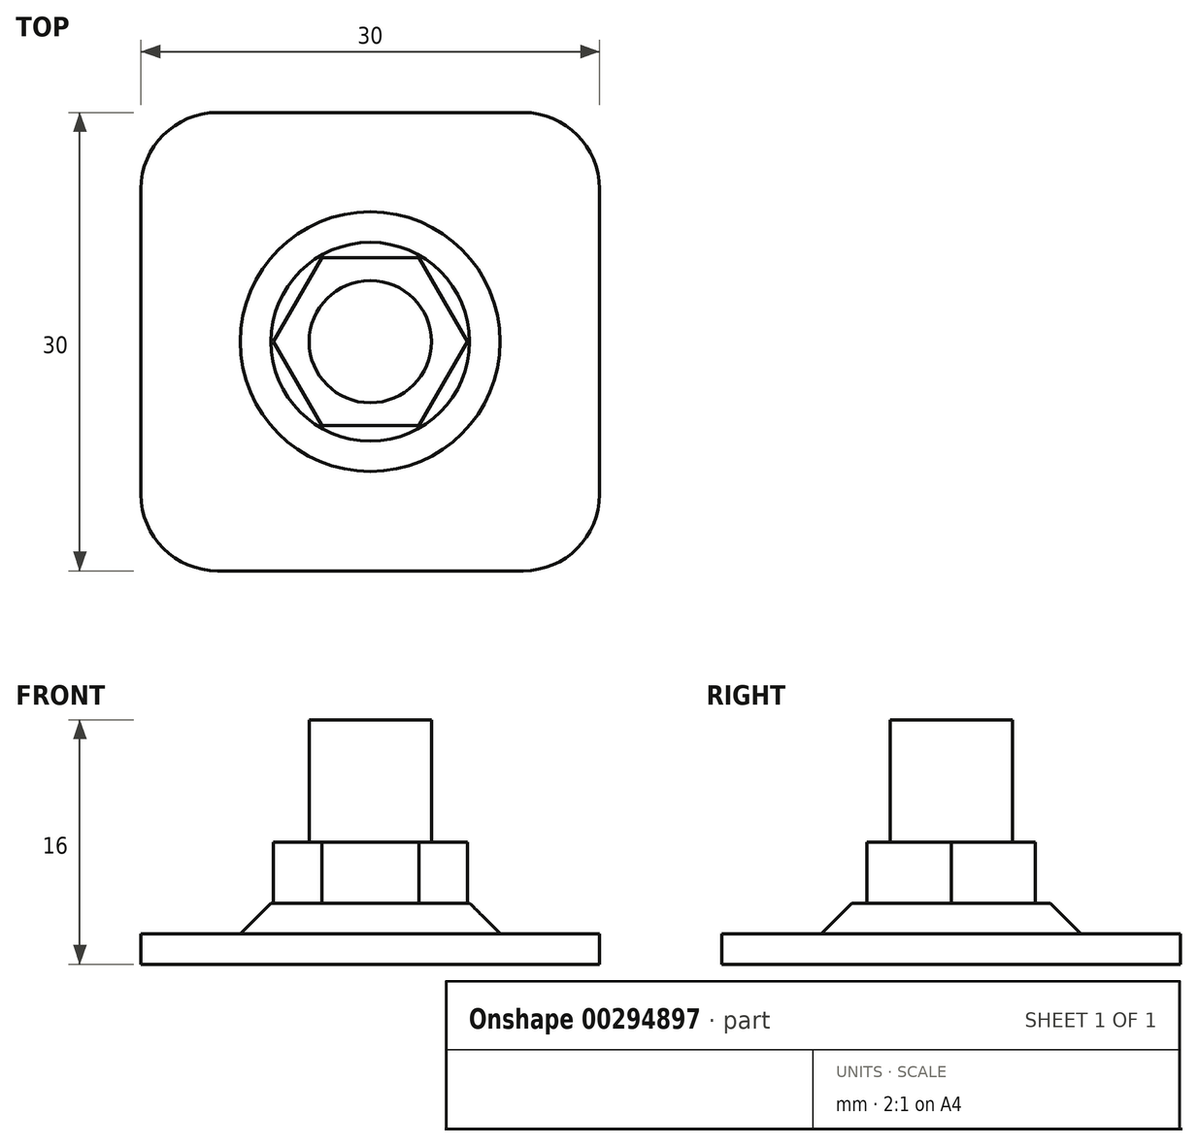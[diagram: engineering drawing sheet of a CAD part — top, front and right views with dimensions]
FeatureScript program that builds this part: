
annotation { "Feature Type Name" : "Feature", "Feature Type Description" : "" }
export const myFeature = defineFeature(function(context is Context, id is Id, definition is map)
    precondition{}
    {
        {
            var Q0;
            Q0=qCreatedBy(makeId("Top.planeOp"),FACE);
            var sketch = newSketch(context, id + "F0", { "sketchPlane" : qUnion([Q0])});
            skLineSegment(sketch, "E0.bottom", {"start": v(10, 15) * mm, "end": v(-10, 15) * mm});
            skLineSegment(sketch, "E0.top", {"start": v(10, -15) * mm, "end": v(-10, -15) * mm});
            skLineSegment(sketch, "E0.left", {"start": v(15, 10) * mm, "end": v(15, -10) * mm});
            skLineSegment(sketch, "E0.right", {"start": v(-15, 10) * mm, "end": v(-15, -10) * mm});
            skPoint(sketch, "E0.middle", {"position": v(0, 0) * mm});
            skPoint(sketch, "E1.visualSharp", {"position": v(-15, 15) * mm});
            skArc(sketch, "E1.filletArc", {"start": v(-10, 15) * mm, "mid": v(-13.54, 13.54) * mm, "end": v(-15, 10) * mm});
            skPoint(sketch, "E2.visualSharp", {"position": v(15, 15) * mm});
            skArc(sketch, "E2.filletArc", {"start": v(15, 10) * mm, "mid": v(13.54, 13.54) * mm, "end": v(10, 15) * mm});
            skPoint(sketch, "E3.visualSharp", {"position": v(15, -15) * mm});
            skArc(sketch, "E3.filletArc", {"start": v(10, -15) * mm, "mid": v(13.54, -13.54) * mm, "end": v(15, -10) * mm});
            skPoint(sketch, "E4.visualSharp", {"position": v(-15, -15) * mm});
            skArc(sketch, "E4.filletArc", {"start": v(-15, -10) * mm, "mid": v(-13.54, -13.54) * mm, "end": v(-10, -15) * mm});
            skSolve(sketch);
        }
        {
            var Q0;
            Q0=makeQuery(id+"F0.imprint","IMPRINT",FACE,{"disambiguationData":[TD([[makeQuery(id+"F0.imprint","IMPRINT",EDGE,{"derivedFrom":sQuery(id+"F0.wireOp",EDGE,"E0.bottom")}),1.0]])]});
            extrude(context, id + "F1", {"entities" : qUnion([Q0]), "depth" : 2 * mm});
        }
        {
            var Q0;
            Q0=makeQuery(id+"F1.opExtrude","CAP_FACE",FACE,{"disambiguationData":[OSD([sQuery(id+"F0.wireOp",EDGE,"E0.bottom"),sQuery(id+"F0.wireOp",EDGE,"E0.top"),sQuery(id+"F0.wireOp",EDGE,"E0.left"),sQuery(id+"F0.wireOp",EDGE,"E0.right"),sQuery(id+"F0.wireOp",EDGE,"E1.filletArc"),sQuery(id+"F0.wireOp",EDGE,"E2.filletArc"),sQuery(id+"F0.wireOp",EDGE,"E3.filletArc"),sQuery(id+"F0.wireOp",EDGE,"E4.filletArc")])],"isStart":false});
            var sketch = newSketch(context, id + "F2", { "sketchPlane" : qUnion([Q0])});
            skCircle(sketch, "E5", {"center": v(0, 0) * mm, "radius": 8.5 * mm});
            skSolve(sketch);
        }
        {
            var Q0;
            Q0=makeQuery(id+"F2.imprint","IMPRINT",FACE,{"disambiguationData":[TD([[makeQuery(id+"F2.imprint","IMPRINT",EDGE,{"derivedFrom":sQuery(id+"F2.wireOp",EDGE,"E5")}),1.0]])]});
            extrude(context, id + "F3", {"entities" : qUnion([Q0]), "operationType" : NewBodyOperationType.ADD, "depth" : 2 * mm});
        }
        {
            var Q0;
            Q0=makeQuery(id+"F3.opExtrude","CAP_EDGE",EDGE,{"disambiguationData":[OSD([sQuery(id+"F2.wireOp",EDGE,"E5")])],"isStart":false});
            chamfer(context, id + "F4", {"entities" : qUnion([Q0]), "width" : 2 * mm, "tangentPropagation" : true});
        }
        {
            var Q0;
            Q0=makeQuery(id+"F3.opExtrude","CAP_FACE",FACE,{"disambiguationData":[OSD([sQuery(id+"F2.wireOp",EDGE,"E5")])],"isStart":false});
            var sketch = newSketch(context, id + "F5", { "sketchPlane" : qUnion([Q0])});
            skCircle(sketch, "E6.cCircle", {"center": v(0, 0) * mm, "radius": 5.5 * mm, "construction": true});
            skLineSegment(sketch, "E6.0", {"start": v(3.18, 5.5) * mm, "end": v(6.35, 0) * mm});
            skLineSegment(sketch, "E6.1", {"start": v(6.35, 0) * mm, "end": v(3.18, -5.5) * mm});
            skLineSegment(sketch, "E6.2", {"start": v(3.18, -5.5) * mm, "end": v(-3.18, -5.5) * mm});
            skLineSegment(sketch, "E6.3", {"start": v(-3.18, -5.5) * mm, "end": v(-6.35, 0) * mm});
            skLineSegment(sketch, "E6.4", {"start": v(-6.35, 0) * mm, "end": v(-3.18, 5.5) * mm});
            skLineSegment(sketch, "E6.5", {"start": v(-3.18, 5.5) * mm, "end": v(3.18, 5.5) * mm});
            skPoint(sketch, "E6.0.midPoint", {"position": v(4.76, 2.75) * mm});
            skSolve(sketch);
        }
        {
            var Q0;
            Q0 = qSketchRegion(id + "F5", true);
            extrude(context, id + "F6", {"entities" : qUnion([Q0]), "operationType" : NewBodyOperationType.ADD, "depth" : 4 * mm});
        }
        {
            var Q0;
            Q0=makeQuery(id+"F6.opExtrude","CAP_FACE",FACE,{"disambiguationData":[OSD([sQuery(id+"F5.wireOp",EDGE,"E6.0"),sQuery(id+"F5.wireOp",EDGE,"E6.1"),sQuery(id+"F5.wireOp",EDGE,"E6.2"),sQuery(id+"F5.wireOp",EDGE,"E6.3"),sQuery(id+"F5.wireOp",EDGE,"E6.4"),sQuery(id+"F5.wireOp",EDGE,"E6.5")])],"isStart":false});
            var sketch = newSketch(context, id + "F7", { "sketchPlane" : qUnion([Q0])});
            skCircle(sketch, "E7", {"center": v(0, 0) * mm, "radius": 4 * mm});
            skSolve(sketch);
        }
        {
            var Q0;
            Q0 = qSketchRegion(id + "F7", true);
            extrude(context, id + "F8", {"entities" : qUnion([Q0]), "operationType" : NewBodyOperationType.ADD, "depth" : 8 * mm});
        }
    });
